# Revit family: TD92_ZUM126_AMA000_RVT20_R00
name_source: partatom
category: Mobiliário
units: mm (PartAtom-declared; Revit-internal decimal feet)

## family parameters
Com base no plano de trabalho = Não
Compartilhado = Não
Corte com vazios quando carregada = Não
Número OmniClass = 23.40.20.00
Ponto de cálculo do ambiente = Não
Sempre na vertical = Sim
Título OmniClass = General Furniture and Specialties

## types (1)
- TD92_ZUM126_AMA000_RVT20_R00
    Descrição = A Gangorra Ponte Infantil Tramontina Zum em Polietileno vai levar muito mais alegria e descontração para o dia a dia das crianças. Produzida em polietileno livre de toxinas, ela possui um design minimalista de ponte, mas conta com cores super vibrantes e alegres que vão se destacar em meio a todos os brinquedos e deixar os pequenos ainda mais felizes, pois é muito versátil e pode ser utilizada como gangorra ou como ponte para escalada. A escolha perfeita para ser inserida nos playgrounds de casas, condomínios ou ambientes comerciais!
    Elevação padrão = 0  [stored 0 ft]
    Fabricante = Tramontina Delta S/A
    Modelo = Gangorra Ponte Infantil Tramontina Zum em Polietileno Amarelo
    Nota-chave = 92126000
    URL = https://www.tramontinastore.com

note: [stored X ft] marks values corroborated as IEEE doubles in the binary element streams (Revit-internal decimal feet)
